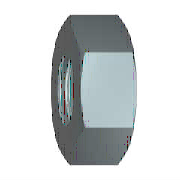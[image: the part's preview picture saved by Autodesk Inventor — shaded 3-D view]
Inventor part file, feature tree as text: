
AUTODESK INVENTOR PART (.ipt)
format: ipt  version: 2013 (Build 170138000, 138)  size: 171,520 bytes
history: native  units: mm (DEFAULTED — no unit token found)
features: sketch x3, chamfer x1, hole x1, other x1, plane x1
ambient origin geometry x7: Origin, YZ Plane, XZ Plane, X Axis, Y Axis, Z Axis, Center Point
bodies: Solid1 (feature_tree), Body (feature_tree)
feature tree (7):
  chamfer  "Chamfer1"  Distance=4.363323mm
  hole  "Thread"  [1 undecoded]
  other  "Work Axis1"
  plane  "Work Plane1"
  sketch  "Sketch1"  dims[d0=15.011107mm]
  sketch  "Sketch2"  dims[d1=6.8mm]
  sketch  "Sketch3"  dims[d2=0.0mm d3=4.363323mm d4=4.363323mm d5=13.0mm d6=13.0mm d7=90.0deg d25=6.647mm d26=6.0mm d27=4.0mm d28=2.0mm d29=14.3117mm d30=8.0mm d31=20.594885mm d8=0.676582mm d9=30.0deg d10=0.676582mm d11=30.0deg d13=0.0mm d14=0.0mm d39=0.0mm d40=0.676582mm d41=0.676582mm d42=0.0mm]
note: 1 required parameter value undecoded (feature->parameter linkage not recoverable at this tier; creation-order binding heuristic only, values carry confidence <= 0.55)
